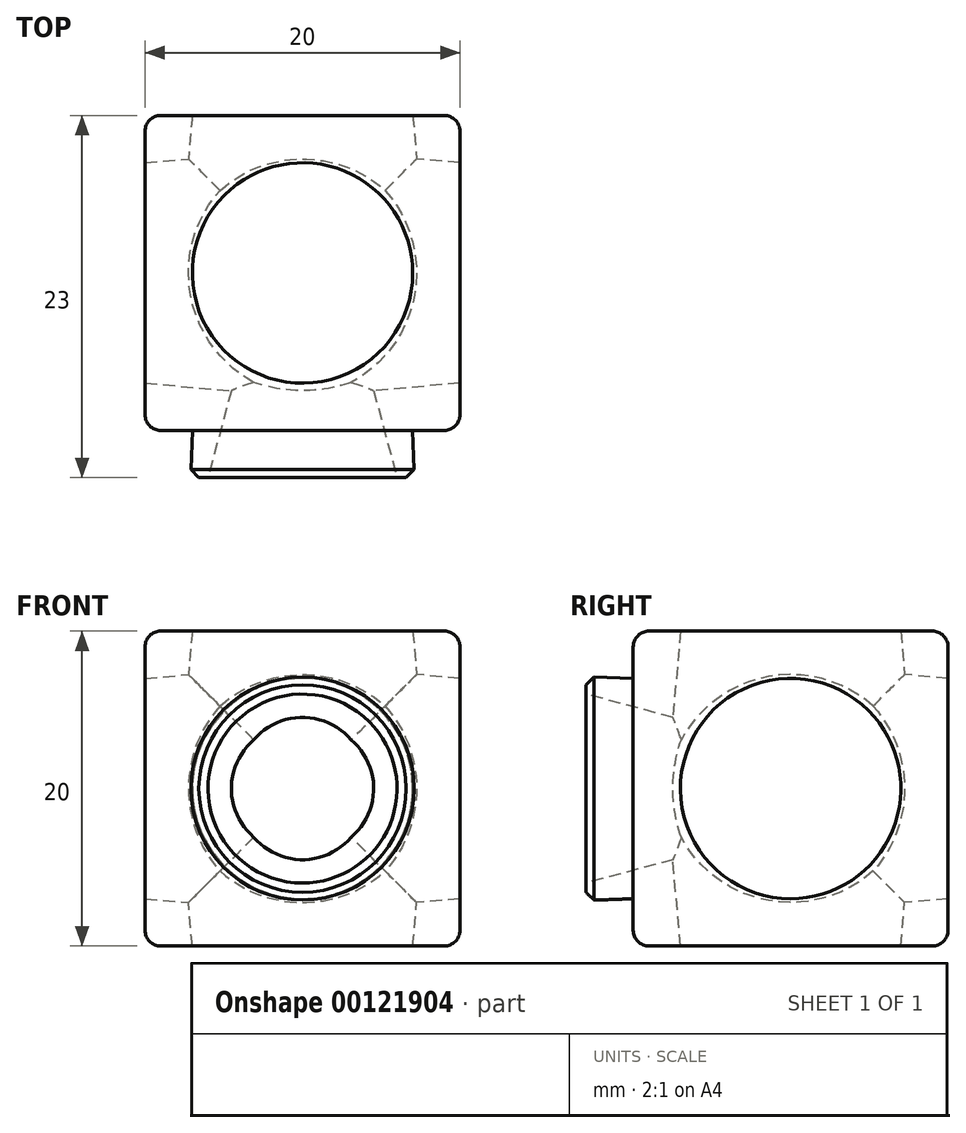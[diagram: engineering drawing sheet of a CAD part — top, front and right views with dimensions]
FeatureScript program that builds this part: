
annotation { "Feature Type Name" : "Feature", "Feature Type Description" : "" }
export const myFeature = defineFeature(function(context is Context, id is Id, definition is map)
    precondition{}
    {
        {
            var Q0;
            Q0=qCreatedBy(makeId("Top.planeOp"),FACE);
            var sketch = newSketch(context, id + "F0", { "sketchPlane" : qUnion([Q0])});
            skLineSegment(sketch, "E0.bottom", {"start": v(0, 0) * mm, "end": v(20, 0) * mm});
            skLineSegment(sketch, "E0.top", {"start": v(0, 20) * mm, "end": v(20, 20) * mm});
            skLineSegment(sketch, "E0.left", {"start": v(0, 0) * mm, "end": v(0, 20) * mm});
            skLineSegment(sketch, "E0.right", {"start": v(20, 0) * mm, "end": v(20, 20) * mm});
            skSolve(sketch);
        }
        {
            var Q0;
            Q0=makeQuery(id+"F0.imprint","IMPRINT",FACE,{"disambiguationData":[TD([[makeQuery(id+"F0.imprint","IMPRINT",EDGE,{"derivedFrom":sQuery(id+"F0.wireOp",EDGE,"E0.bottom")}),1.0]])]});
            extrude(context, id + "F1", {"entities" : qUnion([Q0]), "depth" : 20 * mm});
        }
        {
            var Q0;
            Q0=makeQuery(id+"F1.opExtrude","CAP_FACE",FACE,{"disambiguationData":[OSD([sQuery(id+"F0.wireOp",EDGE,"E0.bottom"),sQuery(id+"F0.wireOp",EDGE,"E0.top"),sQuery(id+"F0.wireOp",EDGE,"E0.left"),sQuery(id+"F0.wireOp",EDGE,"E0.right")])],"isStart":false});
            var sketch = newSketch(context, id + "F2", { "sketchPlane" : qUnion([Q0])});
            skPoint(sketch, "E1", {"position": v(10, 20) * mm});
            skPoint(sketch, "E2", {"position": v(20, 10) * mm});
            skCircle(sketch, "E3", {"center": v(10, 10) * mm, "radius": 7 * mm});
            skSolve(sketch);
        }
        {
            var Q0;
            Q0=makeQuery(id+"F2.imprint","IMPRINT",FACE,{"disambiguationData":[TD([[makeQuery(id+"F2.imprint","IMPRINT",EDGE,{"derivedFrom":sQuery(id+"F2.wireOp",EDGE,"E3")}),1.0]])]});
            extrude(context, id + "F3", {"entities" : qUnion([Q0]), "operationType" : NewBodyOperationType.REMOVE, "oppositeDirection" : true, "depth" : 10 * mm, "hasDraft" : true, "draftAngle" : 5 * degree});
        }
        {
            var Q0;
            Q0=makeQuery(id+"F1.opExtrude","SWEPT_FACE",FACE,{"disambiguationData":[OSD([sQuery(id+"F0.wireOp",EDGE,"E0.right")])]});
            var sketch = newSketch(context, id + "F4", { "sketchPlane" : qUnion([Q0])});
            skPoint(sketch, "E4", {"position": v(10, 20) * mm});
            skPoint(sketch, "E5", {"position": v(20, 10) * mm});
            skCircle(sketch, "E6", {"center": v(10, 10) * mm, "radius": 7 * mm});
            skSolve(sketch);
        }
        {
            var Q0;
            Q0=makeQuery(id+"F4.imprint","IMPRINT",FACE,{"disambiguationData":[TD([[makeQuery(id+"F4.imprint","IMPRINT",EDGE,{"derivedFrom":sQuery(id+"F4.wireOp",EDGE,"E6")}),1.0]])]});
            extrude(context, id + "F5", {"entities" : qUnion([Q0]), "operationType" : NewBodyOperationType.REMOVE, "oppositeDirection" : true, "depth" : 10 * mm, "hasDraft" : true, "draftAngle" : 5 * degree});
        }
        {
            var Q0;
            Q0=makeQuery(id+"F1.opExtrude","SWEPT_FACE",FACE,{"disambiguationData":[OSD([sQuery(id+"F0.wireOp",EDGE,"E0.top")])]});
            var sketch = newSketch(context, id + "F6", { "sketchPlane" : qUnion([Q0])});
            skPoint(sketch, "E7", {"position": v(-10, 20) * mm});
            skPoint(sketch, "E8", {"position": v(0, 10) * mm});
            skCircle(sketch, "E9", {"center": v(-10, 10) * mm, "radius": 7 * mm});
            skSolve(sketch);
        }
        {
            var Q0;
            Q0=makeQuery(id+"F6.imprint","IMPRINT",FACE,{"disambiguationData":[TD([[makeQuery(id+"F6.imprint","IMPRINT",EDGE,{"derivedFrom":sQuery(id+"F6.wireOp",EDGE,"E9")}),1.0]])]});
            extrude(context, id + "F7", {"entities" : qUnion([Q0]), "operationType" : NewBodyOperationType.REMOVE, "oppositeDirection" : true, "depth" : 10 * mm, "hasDraft" : true, "draftAngle" : 5 * degree});
        }
        {
            var Q0;
            Q0=makeQuery(id+"F1.opExtrude","SWEPT_FACE",FACE,{"disambiguationData":[OSD([sQuery(id+"F0.wireOp",EDGE,"E0.left")])]});
            var sketch = newSketch(context, id + "F8", { "sketchPlane" : qUnion([Q0])});
            skPoint(sketch, "E10", {"position": v(-10, 20) * mm});
            skPoint(sketch, "E11", {"position": v(0, 10) * mm});
            skCircle(sketch, "E12", {"center": v(-10, 10) * mm, "radius": 7 * mm});
            skSolve(sketch);
        }
        {
            var Q0;
            Q0=makeQuery(id+"F8.imprint","IMPRINT",FACE,{"disambiguationData":[TD([[makeQuery(id+"F8.imprint","IMPRINT",EDGE,{"derivedFrom":sQuery(id+"F8.wireOp",EDGE,"E12")}),1.0]])]});
            extrude(context, id + "F9", {"entities" : qUnion([Q0]), "operationType" : NewBodyOperationType.REMOVE, "oppositeDirection" : true, "depth" : 10 * mm, "hasDraft" : true, "draftAngle" : 5 * degree});
        }
        {
            var Q0;
            Q0=makeQuery(id+"F1.opExtrude","CAP_FACE",FACE,{"disambiguationData":[OSD([sQuery(id+"F0.wireOp",EDGE,"E0.bottom"),sQuery(id+"F0.wireOp",EDGE,"E0.top"),sQuery(id+"F0.wireOp",EDGE,"E0.left"),sQuery(id+"F0.wireOp",EDGE,"E0.right")])],"isStart":true});
            var sketch = newSketch(context, id + "F10", { "sketchPlane" : qUnion([Q0])});
            skPoint(sketch, "E13", {"position": v(10, 0) * mm});
            skPoint(sketch, "E14", {"position": v(20, -10) * mm});
            skCircle(sketch, "E15", {"center": v(10, -10) * mm, "radius": 7 * mm});
            skSolve(sketch);
        }
        {
            var Q0;
            Q0=makeQuery(id+"F10.imprint","IMPRINT",FACE,{"disambiguationData":[TD([[makeQuery(id+"F10.imprint","IMPRINT",EDGE,{"derivedFrom":sQuery(id+"F10.wireOp",EDGE,"E15")}),1.0]])]});
            extrude(context, id + "F11", {"entities" : qUnion([Q0]), "operationType" : NewBodyOperationType.REMOVE, "oppositeDirection" : true, "depth" : 10 * mm, "hasDraft" : true, "draftAngle" : 5 * degree});
        }
        {
            var Q0;
            Q0=makeQuery(id+"F1.opExtrude","SWEPT_FACE",FACE,{"disambiguationData":[OSD([sQuery(id+"F0.wireOp",EDGE,"E0.bottom")])]});
            var sketch = newSketch(context, id + "F12", { "sketchPlane" : qUnion([Q0])});
            skPoint(sketch, "E16", {"position": v(10, 20) * mm});
            skPoint(sketch, "E17", {"position": v(20, 10) * mm});
            skCircle(sketch, "E18", {"center": v(10, 10) * mm, "radius": 7 * mm});
            skSolve(sketch);
        }
        {
            var Q0;
            Q0=makeQuery(id+"F12.imprint","IMPRINT",FACE,{"disambiguationData":[TD([[makeQuery(id+"F12.imprint","IMPRINT",EDGE,{"derivedFrom":sQuery(id+"F12.wireOp",EDGE,"E18")}),1.0]])]});
            extrude(context, id + "F13", {"entities" : qUnion([Q0]), "operationType" : NewBodyOperationType.ADD, "depth" : 3 * mm, "hasDraft" : true, "draftAngle" : 2 * degree});
        }
        {
            var Q0;
            Q0=makeQuery(id+"F13.opExtrude","CAP_FACE",FACE,{"disambiguationData":[OSD([sQuery(id+"F12.wireOp",EDGE,"E18")])],"isStart":false});
            var sketch = newSketch(context, id + "F14", { "sketchPlane" : qUnion([Q0])});
            skCircle(sketch, "E19", {"center": v(10, 10) * mm, "radius": 6 * mm});
            skSolve(sketch);
        }
        {
            var Q0;
            Q0=makeQuery(id+"F14.imprint","IMPRINT",FACE,{"disambiguationData":[TD([[makeQuery(id+"F14.imprint","IMPRINT",EDGE,{"derivedFrom":sQuery(id+"F14.wireOp",EDGE,"E19")}),1.0]])]});
            extrude(context, id + "F15", {"entities" : qUnion([Q0]), "operationType" : NewBodyOperationType.REMOVE, "oppositeDirection" : true, "depth" : 10 * mm, "hasDraft" : true, "draftAngle" : 15 * degree, "draftPullDirection" : true});
        }
        {
            var Q0;
            Q0=makeQuery(id+"F1.opExtrude","SWEPT_EDGE",EDGE,{"disambiguationData":[OSD([sQuery(id+"F0.wireOp",EDGE,"E0.bottom"),sQuery(id+"F0.wireOp",EDGE,"E0.right")])]});
            var Q1;
            Q1=makeQuery(id+"F1.opExtrude","CAP_EDGE",EDGE,{"disambiguationData":[OSD([sQuery(id+"F0.wireOp",EDGE,"E0.right")])],"isStart":false});
            var Q2;
            Q2=makeQuery(id+"F1.opExtrude","CAP_EDGE",EDGE,{"disambiguationData":[OSD([sQuery(id+"F0.wireOp",EDGE,"E0.bottom")])],"isStart":false});
            var Q3;
            Q3=makeQuery(id+"F1.opExtrude","CAP_EDGE",EDGE,{"disambiguationData":[OSD([sQuery(id+"F0.wireOp",EDGE,"E0.bottom")])],"isStart":true});
            var Q4;
            Q4=makeQuery(id+"F1.opExtrude","CAP_EDGE",EDGE,{"disambiguationData":[OSD([sQuery(id+"F0.wireOp",EDGE,"E0.right")])],"isStart":true});
            var Q5;
            Q5=makeQuery(id+"F1.opExtrude","CAP_EDGE",EDGE,{"disambiguationData":[OSD([sQuery(id+"F0.wireOp",EDGE,"E0.top")])],"isStart":true});
            var Q6;
            Q6=makeQuery(id+"F1.opExtrude","CAP_EDGE",EDGE,{"disambiguationData":[OSD([sQuery(id+"F0.wireOp",EDGE,"E0.left")])],"isStart":true});
            var Q7;
            Q7=makeQuery(id+"F1.opExtrude","SWEPT_EDGE",EDGE,{"disambiguationData":[OSD([sQuery(id+"F0.wireOp",EDGE,"E0.bottom"),sQuery(id+"F0.wireOp",EDGE,"E0.left")])]});
            var Q8;
            Q8=makeQuery(id+"F1.opExtrude","SWEPT_EDGE",EDGE,{"disambiguationData":[OSD([sQuery(id+"F0.wireOp",EDGE,"E0.top"),sQuery(id+"F0.wireOp",EDGE,"E0.left")])]});
            var Q9;
            Q9=makeQuery(id+"F1.opExtrude","CAP_EDGE",EDGE,{"disambiguationData":[OSD([sQuery(id+"F0.wireOp",EDGE,"E0.left")])],"isStart":false});
            var Q10;
            Q10=makeQuery(id+"F1.opExtrude","SWEPT_EDGE",EDGE,{"disambiguationData":[OSD([sQuery(id+"F0.wireOp",EDGE,"E0.top"),sQuery(id+"F0.wireOp",EDGE,"E0.right")])]});
            var Q11;
            Q11=makeQuery(id+"F1.opExtrude","CAP_EDGE",EDGE,{"disambiguationData":[OSD([sQuery(id+"F0.wireOp",EDGE,"E0.top")])],"isStart":false});
            fillet(context, id + "F16", {"entities" : qUnion([Q0, Q1, Q2, Q3, Q4, Q5, Q6, Q7, Q8, Q9, Q10, Q11]), "radius" : 1 * mm, "tangentPropagation" : true, "allowEdgeOverflow" : false});
        }
        {
            var Q0;
            Q0=makeQuery(id+"F13.opExtrude","CAP_EDGE",EDGE,{"disambiguationData":[OSD([sQuery(id+"F12.wireOp",EDGE,"E18")])],"isStart":false});
            var Q1;
            Q1=makeQuery(id+"F11.boolean.opBoolean","COPY",EDGE,{"derivedFrom":makeQuery(id+"F11.opExtrude","CAP_EDGE",EDGE,{"disambiguationData":[OSD([sQuery(id+"F10.wireOp",EDGE,"E15")])],"isStart":true})});
            var Q2;
            Q2=makeQuery(id+"F9.boolean.opBoolean","COPY",EDGE,{"derivedFrom":makeQuery(id+"F9.opExtrude","CAP_EDGE",EDGE,{"disambiguationData":[OSD([sQuery(id+"F8.wireOp",EDGE,"E12")])],"isStart":true})});
            var Q3;
            Q3=makeQuery(id+"F3.boolean.opBoolean","COPY",EDGE,{"derivedFrom":makeQuery(id+"F3.opExtrude","CAP_EDGE",EDGE,{"disambiguationData":[OSD([sQuery(id+"F2.wireOp",EDGE,"E3")])],"isStart":true})});
            var Q4;
            Q4=makeQuery(id+"F5.boolean.opBoolean","COPY",EDGE,{"derivedFrom":makeQuery(id+"F5.opExtrude","CAP_EDGE",EDGE,{"disambiguationData":[OSD([sQuery(id+"F4.wireOp",EDGE,"E6")])],"isStart":true})});
            var Q5;
            Q5=makeQuery(id+"F7.boolean.opBoolean","COPY",EDGE,{"derivedFrom":makeQuery(id+"F7.opExtrude","CAP_EDGE",EDGE,{"disambiguationData":[OSD([sQuery(id+"F6.wireOp",EDGE,"E9")])],"isStart":true})});
            chamfer(context, id + "F17", {"entities" : qUnion([Q0, Q1, Q2, Q3, Q4, Q5]), "width" : 0.5 * mm, "tangentPropagation" : true});
        }
    });
